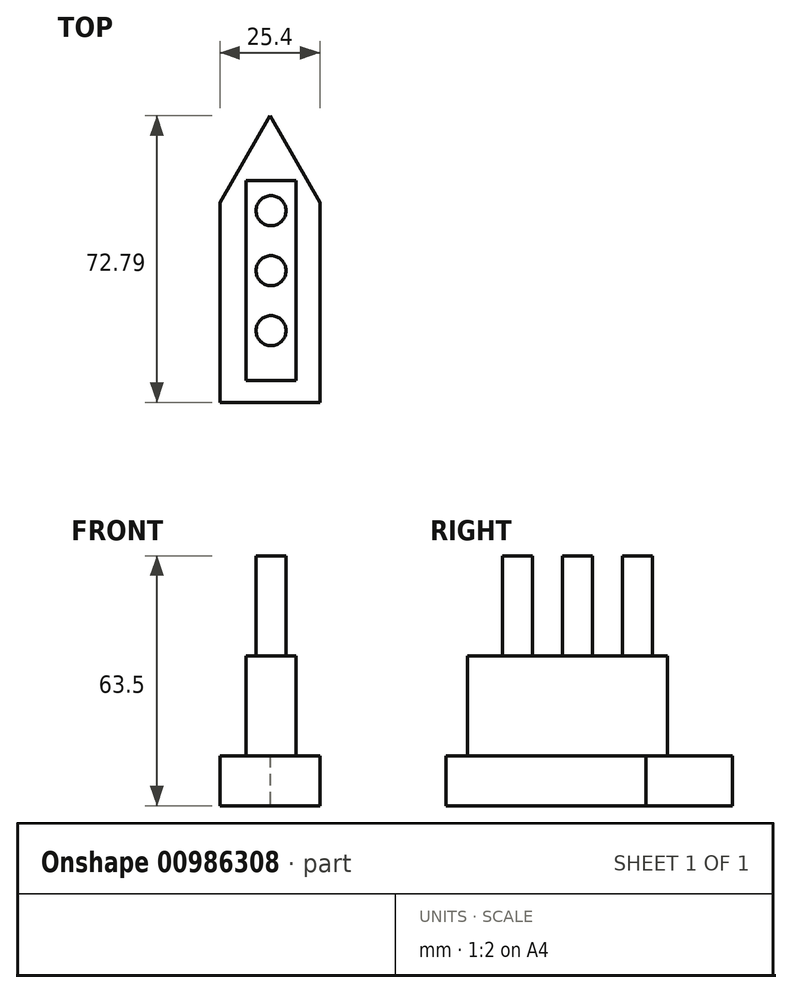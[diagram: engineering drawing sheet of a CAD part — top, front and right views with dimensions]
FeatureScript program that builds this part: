
annotation { "Feature Type Name" : "Feature", "Feature Type Description" : "" }
export const myFeature = defineFeature(function(context is Context, id is Id, definition is map)
    precondition{}
    {
        {
            var Q0;
            Q0=qCreatedBy(makeId("Top.planeOp"),FACE);
            var sketch = newSketch(context, id + "F0", { "sketchPlane" : qUnion([Q0])});
            skLineSegment(sketch, "E0.top", {"start": v(-12.7, -32.55) * mm, "end": v(12.7, -32.55) * mm});
            skLineSegment(sketch, "E0.left", {"start": v(-12.7, 18.25) * mm, "end": v(-12.7, -32.55) * mm});
            skLineSegment(sketch, "E0.right", {"start": v(12.7, 18.25) * mm, "end": v(12.7, -32.55) * mm});
            skLineSegment(sketch, "E1", {"start": v(-12.7, 18.25) * mm, "end": v(0, 40.24) * mm});
            skLineSegment(sketch, "E2", {"start": v(0, 40.24) * mm, "end": v(12.7, 18.25) * mm});
            skSolve(sketch);
        }
        {
            var Q0;
            Q0 = qSketchRegion(id + "F0", true);
            extrude(context, id + "F1", {"entities" : qUnion([Q0]), "depth" : 12.7 * mm, "offsetDistance" : 25.4 * mm});
        }
        {
            var Q0;
            Q0=makeQuery(id+"F1.opExtrude","CAP_FACE",FACE,{"disambiguationData":[OSD([sQuery(id+"F0.wireOp",EDGE,"E0.top"),sQuery(id+"F0.wireOp",EDGE,"E0.left"),sQuery(id+"F0.wireOp",EDGE,"E0.right"),sQuery(id+"F0.wireOp",EDGE,"E1"),sQuery(id+"F0.wireOp",EDGE,"E2")])],"isStart":false});
            var sketch = newSketch(context, id + "F2", { "sketchPlane" : qUnion([Q0])});
            skLineSegment(sketch, "E3.bottom", {"start": v(6.65, 23.73) * mm, "end": v(-6.05, 23.73) * mm});
            skLineSegment(sketch, "E3.top", {"start": v(6.65, -27.07) * mm, "end": v(-6.05, -27.07) * mm});
            skLineSegment(sketch, "E3.left", {"start": v(6.65, 23.73) * mm, "end": v(6.65, -27.07) * mm});
            skLineSegment(sketch, "E3.right", {"start": v(-6.05, 23.73) * mm, "end": v(-6.05, -27.07) * mm});
            skSolve(sketch);
        }
        {
            var Q0;
            Q0 = qSketchRegion(id + "F2", true);
            extrude(context, id + "F3", {"entities" : qUnion([Q0]), "operationType" : NewBodyOperationType.ADD, "depth" : 25.4 * mm, "offsetDistance" : 25.4 * mm});
        }
        {
            var Q0;
            Q0=makeQuery(id+"F3.opExtrude","CAP_FACE",FACE,{"disambiguationData":[OSD([sQuery(id+"F2.wireOp",EDGE,"E3.bottom"),sQuery(id+"F2.wireOp",EDGE,"E3.top"),sQuery(id+"F2.wireOp",EDGE,"E3.left"),sQuery(id+"F2.wireOp",EDGE,"E3.right")])],"isStart":false});
            var sketch = newSketch(context, id + "F4", { "sketchPlane" : qUnion([Q0])});
            skCircle(sketch, "E4", {"center": v(0.3, 16.12) * mm, "radius": 3.81 * mm});
            skCircle(sketch, "E5", {"center": v(0.3, 0.88) * mm, "radius": 3.81 * mm});
            skCircle(sketch, "E6", {"center": v(0.3, -14.36) * mm, "radius": 3.81 * mm});
            skSolve(sketch);
        }
        {
            var Q0;
            Q0 = qSketchRegion(id + "F4", true);
            extrude(context, id + "F5", {"entities" : qUnion([Q0]), "operationType" : NewBodyOperationType.ADD, "depth" : 25.4 * mm, "offsetDistance" : 25.4 * mm});
        }
    });
